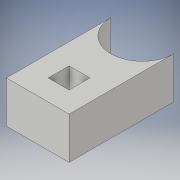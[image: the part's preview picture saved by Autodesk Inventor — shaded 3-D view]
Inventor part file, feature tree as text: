
AUTODESK INVENTOR PART (.ipt)
format: ipt  version: 2019 (Build 230136000, 136)  size: 114,176 bytes
history: native  units: mm
features: sketch x3, extrude x2, other x1, hole x1
ambient origin geometry x8: Origin, YZ Plane, XZ Plane, XY Plane, X Axis, Y Axis, Z Axis, Center Point
bodies: Body1 (feature_tree)
feature tree (7):
  other  "ソリッド1"
  extrude  "押し出し1"  Depth=30.0mm
  hole  "穴1"  [1 undecoded]
  extrude  "押し出し2"  Depth=20.0mm TaperAngle=0.0deg
  sketch  "スケッチ1"
  sketch  "スケッチ2"
  sketch  "スケッチ3"
note: 1 required parameter value undecoded (feature->parameter linkage not recoverable at this tier; creation-order binding heuristic only, values carry confidence <= 0.55)
